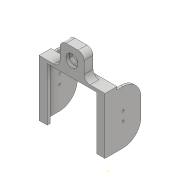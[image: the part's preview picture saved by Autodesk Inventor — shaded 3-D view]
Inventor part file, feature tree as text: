
AUTODESK INVENTOR PART (.ipt)
format: ipt  version: 2017 (Build 210142000, 142)  size: 237,056 bytes
history: native  units: mm
features: sketch x10, projected_geometry x9, extrude x7, fillet x3, hole x2, mirror x1
ambient origin geometry x8: Origin, YZ Plane, XZ Plane, XY Plane, X Axis, Y Axis, Z Axis, Center Point
bodies: Solid1 (feature_tree)
feature tree (32):
  extrude  "Extrusion1"  Depth=20.5mm
  extrude  "Extrusion2"  Depth=11.0mm TaperAngle=0.0deg
  mirror  "Mirror1"
  extrude  "Extrusion3"  Depth=1.0mm TaperAngle=0.0deg
  extrude  "Extrusion4"  Depth=2.0mm
  sketch  "Sketch5"  dims[d11=1.0mm d12=0.0mm d14=27.0mm]
  extrude  "Extrusion5"  Depth=27.0mm
  hole  "Hole1"  [1 undecoded]
  extrude  "Extrusion6"  Depth=6.0mm
  extrude  "Extrusion7"  Depth=3.0mm
  hole  "Hole2"  [1 undecoded]
  fillet  "Fillet3"  [1 undecoded]
  fillet  "Fillet4"  Radius=8.0mm
  fillet  "Fillet5"  Radius=3.0mm
  sketch  "Sketch1"  dims[d0=20.5mm d1=44.0mm]
  sketch  "Sketch2"  dims[d2=22.0mm d3=11.0mm d4=0.0mm]
  projected_geometry  "Projected Loop1"
  projected_geometry  "Projected Loop2"
  sketch  "Sketch3"  dims[d5=3.0mm d6=1.0mm d7=0.0mm]
  projected_geometry  "Projected Loop3"
  sketch  "Sketch4"  dims[d9=2.0mm d10=2.0mm]
  projected_geometry  "Projected Loop4"
  sketch  "Sketch6"  dims[d15=1.0mm d16=0.0mm d17=1.0mm d18=0.0mm]
  projected_geometry  "Projected Loop5"
  sketch  "Sketch7"  dims[d19=6.0mm d20=6.0mm]
  sketch  "Sketch8"  dims[d21=8.0mm d22=3.0mm]
  projected_geometry  "Projected Loop6"
  sketch  "Sketch9"  dims[d23=0.7mm d24=6.0mm d25=4.0mm d26=2.0mm d27=90.0deg d28=8.0mm d29=20.594885mm d30=8.0mm d31=0.0mm d32=8.0mm d33=3.0mm d34=0.0mm]
  projected_geometry  "Projected Loop7"
  projected_geometry  "Projected Loop8"
  sketch  "Sketch10"  dims[d35=5.5mm d36=3.0mm d37=0.0mm d38=4.0mm d39=4.0mm d40=6.0mm d41=4.0mm d42=2.0mm d43=90.0deg d44=8.0mm d45=20.594885mm d46=2.0mm d47=2.0mm d48=6.0mm]
  projected_geometry  "Projected Loop9"
note: 3 required parameter values undecoded (feature->parameter linkage not recoverable at this tier; creation-order binding heuristic only, values carry confidence <= 0.55)
